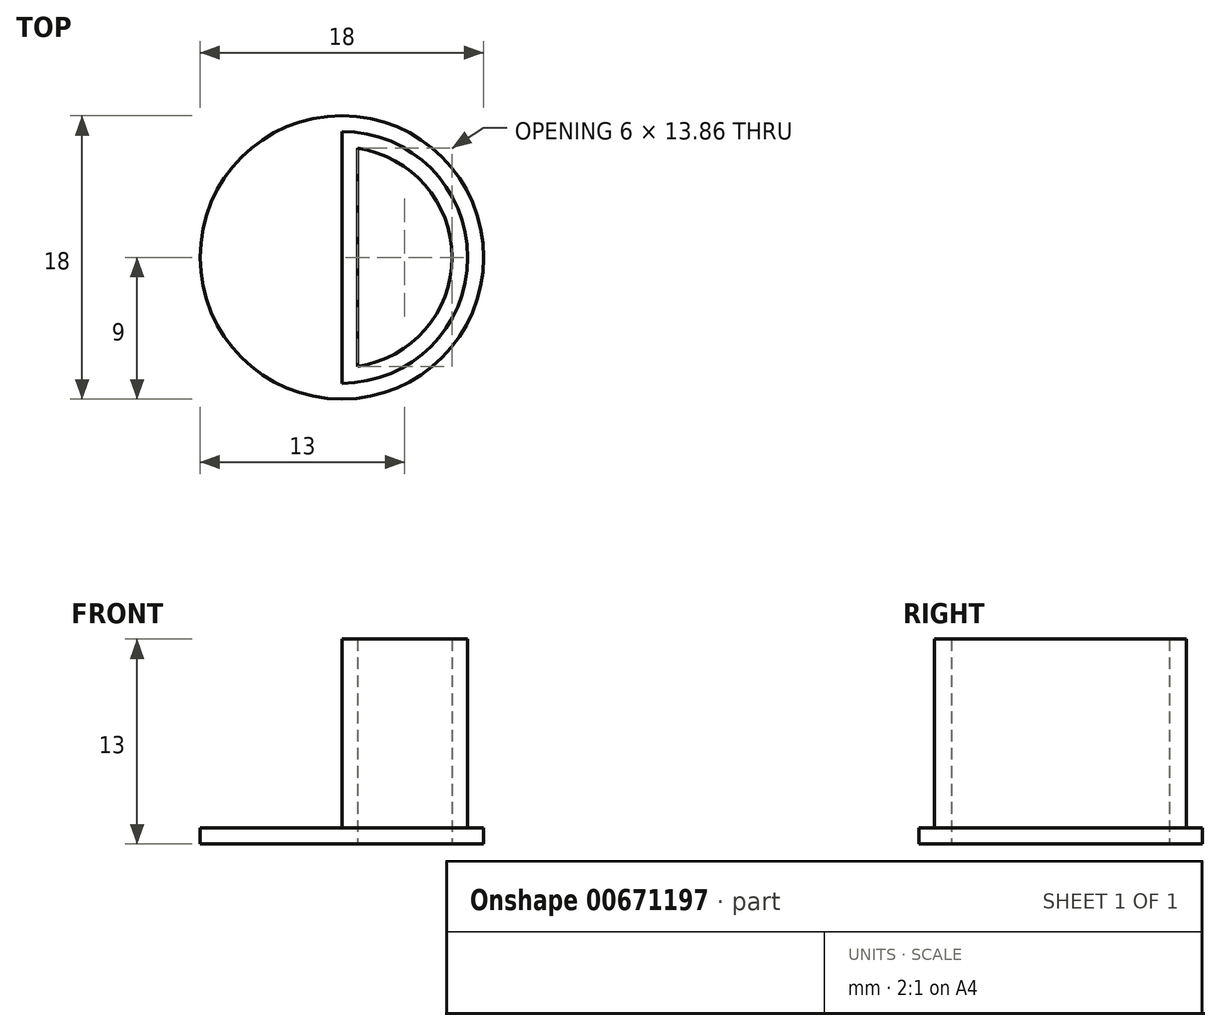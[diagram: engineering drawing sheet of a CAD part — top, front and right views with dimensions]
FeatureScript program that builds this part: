
annotation { "Feature Type Name" : "Feature", "Feature Type Description" : "" }
export const myFeature = defineFeature(function(context is Context, id is Id, definition is map)
    precondition{}
    {
        {
            var Q0;
            Q0=qCreatedBy(makeId("Top.planeOp"),FACE);
            var sketch = newSketch(context, id + "F0", { "sketchPlane" : qUnion([Q0])});
            skCircle(sketch, "E0", {"center": v(0, 0) * mm, "radius": 9 * mm});
            skArc(sketch, "E1", {"start": v(0, -8) * mm, "mid": v(8, 0) * mm, "end": v(0, 8) * mm});
            skLineSegment(sketch, "E2", {"start": v(0, 8) * mm, "end": v(0, -8) * mm});
            skArc(sketch, "E3.0", {"start": v(1, -6.93) * mm, "mid": v(7, 0) * mm, "end": v(1, 6.93) * mm});
            skLineSegment(sketch, "E3.1", {"start": v(1, 6.93) * mm, "end": v(1, -6.93) * mm});
            skSolve(sketch);
        }
        {
            var Q0;
            Q0=makeQuery(id+"F0.imprint","IMPRINT",FACE,{"disambiguationData":[TD([[makeQuery(id+"F0.imprint","IMPRINT",EDGE,{"derivedFrom":sQuery(id+"F0.wireOp",EDGE,"E1")}),1.0]])]});
            extrude(context, id + "F1", {"entities" : qUnion([Q0]), "depth" : 13 * mm, "offsetDistance" : 25 * mm});
        }
        {
            var Q0;
            Q0 = qSketchRegion(id + "F0", true);
            extrude(context, id + "F2", {"entities" : qUnion([Q0]), "operationType" : NewBodyOperationType.ADD, "depth" : 1 * mm, "offsetDistance" : 25 * mm});
        }
    });
